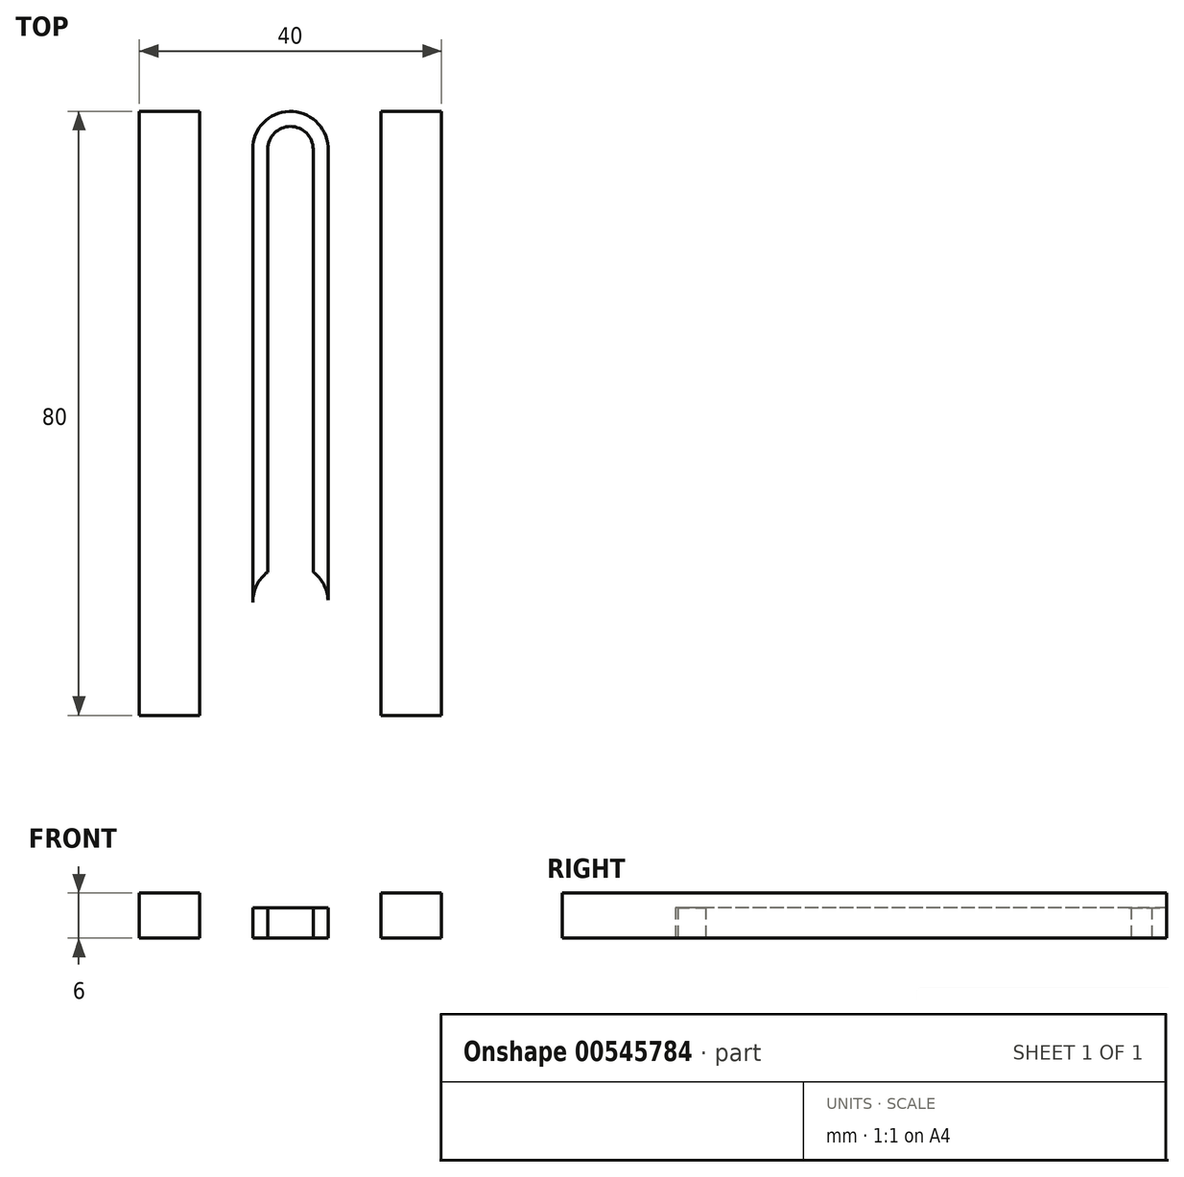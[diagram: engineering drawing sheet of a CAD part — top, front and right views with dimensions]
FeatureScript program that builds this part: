
annotation { "Feature Type Name" : "Feature", "Feature Type Description" : "" }
export const myFeature = defineFeature(function(context is Context, id is Id, definition is map)
    precondition{}
    {
        {
            var Q0;
            Q0=qCreatedBy(makeId("Top.planeOp"),FACE);
            var sketch = newSketch(context, id + "F0", { "sketchPlane" : qUnion([Q0])});
            skLineSegment(sketch, "E0.bottom", {"start": v(20, 50) * mm, "end": v(-20, 50) * mm});
            skLineSegment(sketch, "E0.top", {"start": v(20, -50) * mm, "end": v(-20, -50) * mm});
            skLineSegment(sketch, "E0.left", {"start": v(20, 50) * mm, "end": v(20, -50) * mm});
            skLineSegment(sketch, "E0.right", {"start": v(-20, 50) * mm, "end": v(-20, -50) * mm});
            skPoint(sketch, "E0.middle", {"position": v(0, 0) * mm});
            skLineSegment(sketch, "E1", {"start": v(0, 0) * mm, "end": v(0, -35) * mm, "construction": true});
            skLineSegment(sketch, "E2", {"start": v(0, 0) * mm, "end": v(0, 25) * mm, "construction": true});
            skCircle(sketch, "E3", {"center": v(0, 25) * mm, "radius": 3 * mm});
            skCircle(sketch, "E4", {"center": v(0, -35) * mm, "radius": 3 * mm});
            skLineSegment(sketch, "E5.bottom", {"start": v(-20, 50) * mm, "end": v(20, 50) * mm});
            skLineSegment(sketch, "E5.left", {"start": v(-20, 50) * mm, "end": v(-20, 30) * mm});
            skLineSegment(sketch, "E5.right", {"start": v(20, 50) * mm, "end": v(20, 30) * mm});
            skLineSegment(sketch, "E6.bottom", {"start": v(-20, 30) * mm, "end": v(-12, 30) * mm});
            skLineSegment(sketch, "E6.top", {"start": v(-20, -50) * mm, "end": v(-12, -50) * mm});
            skLineSegment(sketch, "E6.left", {"start": v(-20, 30) * mm, "end": v(-20, -50) * mm});
            skLineSegment(sketch, "E6.right", {"start": v(-12, 30) * mm, "end": v(-12, -50) * mm});
            skLineSegment(sketch, "E7.bottom", {"start": v(20, 30) * mm, "end": v(12, 30) * mm});
            skLineSegment(sketch, "E7.top", {"start": v(20, -50) * mm, "end": v(12, -50) * mm});
            skLineSegment(sketch, "E7.left", {"start": v(20, 30) * mm, "end": v(20, -50) * mm});
            skLineSegment(sketch, "E7.right", {"start": v(12, 30) * mm, "end": v(12, -50) * mm});
            skCircle(sketch, "E8", {"center": v(0, 25) * mm, "radius": 5 * mm});
            skCircle(sketch, "E9", {"center": v(0, -35) * mm, "radius": 5 * mm});
            skLineSegment(sketch, "E10", {"start": v(-5, 25.27) * mm, "end": v(-5, -35.27) * mm});
            skLineSegment(sketch, "E11", {"start": v(4.99, 25.37) * mm, "end": v(4.99, -35.37) * mm});
            skLineSegment(sketch, "E12", {"start": v(-3, 25) * mm, "end": v(-3, -35.27) * mm});
            skLineSegment(sketch, "E13", {"start": v(3, -35.04) * mm, "end": v(3, 25.37) * mm});
            skSolve(sketch);
        }
        {
            var Q0;
            Q0=makeQuery(id+"F0.imprint","IMPRINT",FACE,{"disambiguationData":[TD([[makeQuery(id+"F0.imprint","IMPRINT",EDGE,{"derivedFrom":sQuery(id+"F0.wireOp",EDGE,"E0.top")}),-1.0]])]});
            extrude(context, id + "F1", {"entities" : qUnion([Q0]), "depth" : 6 * mm, "offsetDistance" : 25 * mm});
        }
        {
            var Q0;
            {var subQ8=sQuery(id+"F0.wireOp",EDGE,"E12");var subQ10=sQuery(id+"F0.wireOp",EDGE,"E3");var subQ13=makeQuery(id+"F0.imprint","INTERSECT",VERTEX,{"derivedFrom":[subQ10,subQ8]});Q0=makeQuery(id+"F0.imprint","IMPRINT",FACE,{"disambiguationData":[TD([[makeQuery(id+"F0.imprint","IMPRINT",EDGE,{"disambiguationData":[TD([[subQ13,1.0]])],"derivedFrom":subQ10}),-1.0]])]});}
            var Q1;
            {var subQ0=sQuery(id+"F0.wireOp",EDGE,"E10");var subQ1=sQuery(id+"F0.wireOp",EDGE,"E8");var subQ2=makeQuery(id+"F0.imprint","INTERSECT",VERTEX,{"disambiguationData":[OD(1.0)],"derivedFrom":[subQ1,subQ0]});Q1=makeQuery(id+"F0.imprint","IMPRINT",FACE,{"disambiguationData":[TD([[makeQuery(id+"F0.imprint","IMPRINT",EDGE,{"disambiguationData":[TD([[subQ2,-1.0]])],"derivedFrom":subQ1}),-1.0]])]});}
            var Q2;
            {var subQ0=sQuery(id+"F0.wireOp",EDGE,"E13");var subQ1=sQuery(id+"F0.wireOp",EDGE,"E8");var subQ2=makeQuery(id+"F0.imprint","INTERSECT",VERTEX,{"derivedFrom":[subQ1,subQ0]});Q2=makeQuery(id+"F0.imprint","IMPRINT",FACE,{"disambiguationData":[TD([[makeQuery(id+"F0.imprint","IMPRINT",EDGE,{"disambiguationData":[TD([[subQ2,-1.0]])],"derivedFrom":subQ1}),-1.0]])]});}
            var Q3;
            {var subQ1=sQuery(id+"F0.wireOp",EDGE,"E4");var subQ9=makeQuery(id+"F0.imprint","IMPRINT",VERTEX,{"derivedFrom":subQ1});Q3=makeQuery(id+"F0.imprint","IMPRINT",FACE,{"disambiguationData":[TD([[makeQuery(id+"F0.imprint","IMPRINT",EDGE,{"disambiguationData":[TD([[subQ9,1.0]])],"derivedFrom":subQ1}),-1.0]])]});}
            extrude(context, id + "F2", {"entities" : qUnion([Q0, Q1, Q2, Q3]), "depth" : 4 * mm, "offsetDistance" : 25 * mm});
        }
    });
